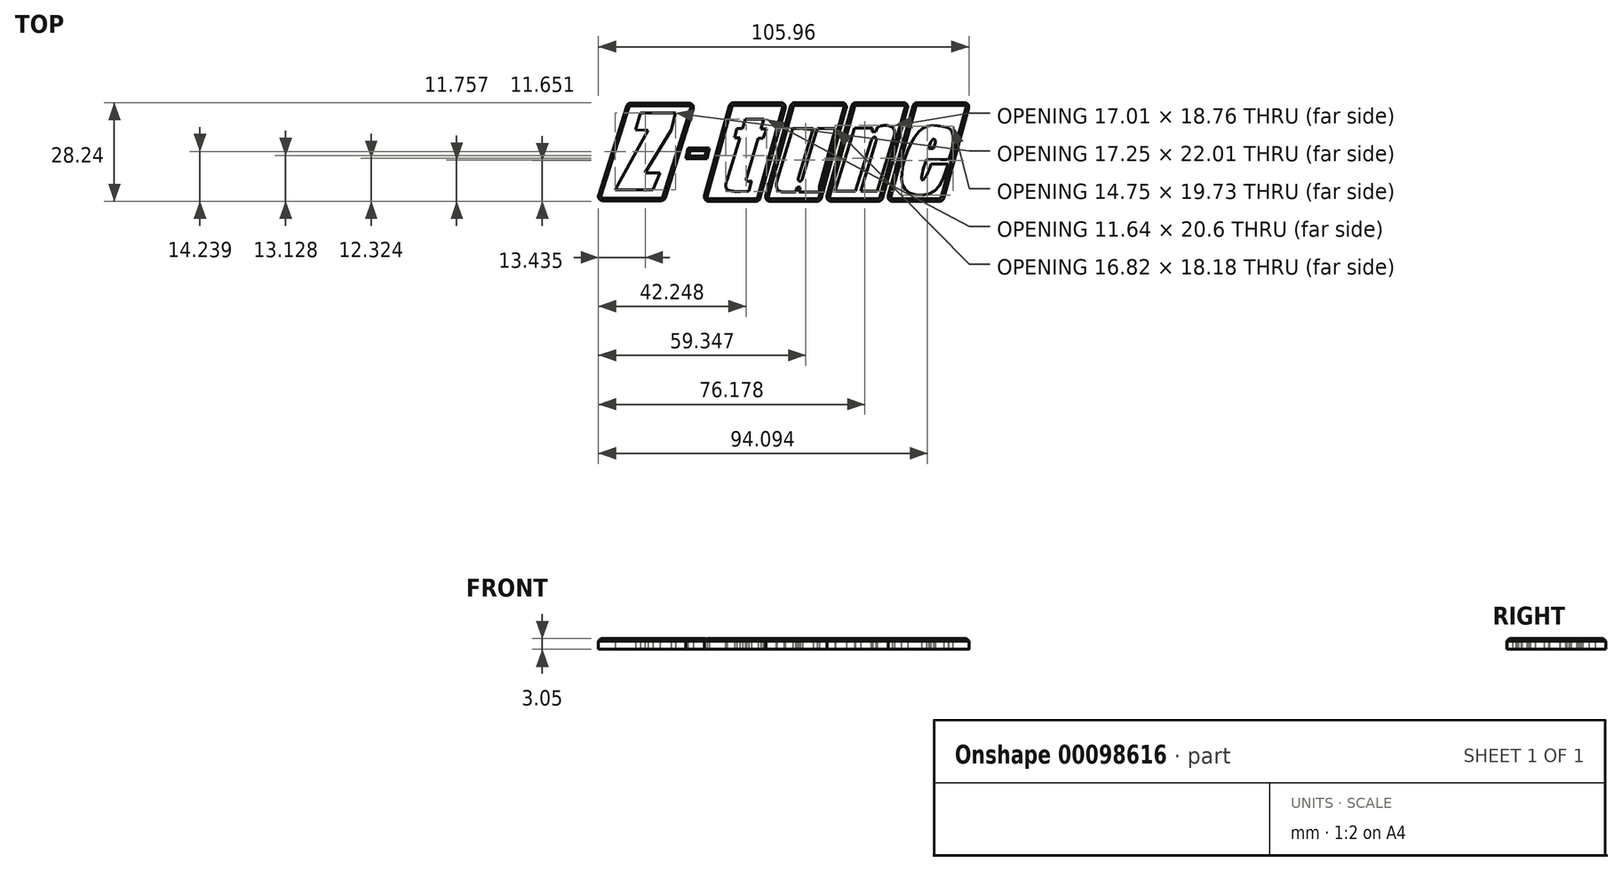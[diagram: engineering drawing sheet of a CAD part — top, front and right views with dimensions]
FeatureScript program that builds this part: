
annotation { "Feature Type Name" : "Feature", "Feature Type Description" : "" }
export const myFeature = defineFeature(function(context is Context, id is Id, definition is map)
    precondition{}
    {
        {
            var Q0;
            Q0=qCreatedBy(makeId("Top.planeOp"),FACE);
            var sketch = newSketch(context, id + "F0", { "sketchPlane" : qUnion([Q0])});
            skLineSegment(sketch, "E0", {"start": v(-41.76, 14.47) * mm, "end": v(-25.09, 14.47) * mm});
            skLineSegment(sketch, "E1", {"start": v(-23.88, 12.82) * mm, "end": v(-31.88, -12.54) * mm});
            skLineSegment(sketch, "E2", {"start": v(-33.1, -13.42) * mm, "end": v(-49.76, -13.42) * mm});
            skLineSegment(sketch, "E3", {"start": v(-50.97, -11.77) * mm, "end": v(-42.97, 13.58) * mm});
            skLineSegment(sketch, "E4", {"start": v(-12.31, 14.64) * mm, "end": v(1.14, 14.64) * mm});
            skLineSegment(sketch, "E5", {"start": v(2.36, 13.03) * mm, "end": v(-4.76, -12.67) * mm});
            skLineSegment(sketch, "E6", {"start": v(-5.99, -13.6) * mm, "end": v(-19.43, -13.6) * mm});
            skLineSegment(sketch, "E7", {"start": v(-20.65, -12) * mm, "end": v(-13.54, 13.7) * mm});
            skPoint(sketch, "E8.visualSharp", {"position": v(-13.28, 14.64) * mm});
            skArc(sketch, "E8.filletArc", {"start": v(-12.31, 14.64) * mm, "mid": v(-13.08, 14.38) * mm, "end": v(-13.54, 13.7) * mm});
            skPoint(sketch, "E9.visualSharp", {"position": v(2.8, 14.64) * mm});
            skArc(sketch, "E9.filletArc", {"start": v(2.36, 13.03) * mm, "mid": v(2.15, 14.14) * mm, "end": v(1.14, 14.64) * mm});
            skPoint(sketch, "E10.visualSharp", {"position": v(-5.02, -13.6) * mm});
            skArc(sketch, "E10.filletArc", {"start": v(-5.99, -13.6) * mm, "mid": v(-5.22, -13.34) * mm, "end": v(-4.76, -12.67) * mm});
            skPoint(sketch, "E11.visualSharp", {"position": v(-21.1, -13.6) * mm});
            skArc(sketch, "E11.filletArc", {"start": v(-20.65, -12) * mm, "mid": v(-20.44, -13.1) * mm, "end": v(-19.43, -13.6) * mm});
            skPoint(sketch, "E12.visualSharp", {"position": v(-23.36, 14.47) * mm});
            skArc(sketch, "E12.filletArc", {"start": v(-23.88, 12.82) * mm, "mid": v(-24.06, 13.95) * mm, "end": v(-25.09, 14.47) * mm});
            skPoint(sketch, "E13.visualSharp", {"position": v(-51.49, -13.42) * mm});
            skArc(sketch, "E13.filletArc", {"start": v(-50.97, -11.77) * mm, "mid": v(-50.78, -12.9) * mm, "end": v(-49.76, -13.42) * mm});
            skPoint(sketch, "E14.visualSharp", {"position": v(-42.7, 14.47) * mm});
            skArc(sketch, "E14.filletArc", {"start": v(-41.76, 14.47) * mm, "mid": v(-42.51, 14.23) * mm, "end": v(-42.97, 13.58) * mm});
            skPoint(sketch, "E15.visualSharp", {"position": v(-32.16, -13.42) * mm});
            skArc(sketch, "E15.filletArc", {"start": v(-33.1, -13.42) * mm, "mid": v(-32.34, -13.18) * mm, "end": v(-31.88, -12.54) * mm});
            skLineSegment(sketch, "E16.1.0.0", {"start": v(19.87, 13.03) * mm, "end": v(12.74, -12.67) * mm});
            skPoint(sketch, "E16.1.0.1", {"position": v(12.49, -13.6) * mm});
            skLineSegment(sketch, "E16.1.0.2", {"start": v(-3.15, -12) * mm, "end": v(3.97, 13.7) * mm});
            skPoint(sketch, "E16.1.0.3", {"position": v(4.23, 14.64) * mm});
            skPoint(sketch, "E16.1.0.4", {"position": v(20.31, 14.64) * mm});
            skLineSegment(sketch, "E16.1.0.5", {"start": v(11.52, -13.6) * mm, "end": v(-1.92, -13.6) * mm});
            skLineSegment(sketch, "E16.1.0.6", {"start": v(5.2, 14.64) * mm, "end": v(18.64, 14.64) * mm});
            skArc(sketch, "E16.1.0.7", {"start": v(-3.15, -12) * mm, "mid": v(-2.93, -13.1) * mm, "end": v(-1.92, -13.6) * mm});
            skArc(sketch, "E16.1.0.8", {"start": v(19.87, 13.03) * mm, "mid": v(19.66, 14.14) * mm, "end": v(18.64, 14.64) * mm});
            skArc(sketch, "E16.1.0.9", {"start": v(5.2, 14.64) * mm, "mid": v(4.42, 14.38) * mm, "end": v(3.97, 13.7) * mm});
            skArc(sketch, "E16.1.0.10", {"start": v(11.52, -13.6) * mm, "mid": v(12.29, -13.34) * mm, "end": v(12.74, -12.67) * mm});
            skLineSegment(sketch, "E16.2.0.0", {"start": v(37.38, 13.03) * mm, "end": v(30.25, -12.67) * mm});
            skPoint(sketch, "E16.2.0.1", {"position": v(30, -13.6) * mm});
            skLineSegment(sketch, "E16.2.0.2", {"start": v(14.36, -12) * mm, "end": v(21.48, 13.7) * mm});
            skPoint(sketch, "E16.2.0.3", {"position": v(21.74, 14.64) * mm});
            skPoint(sketch, "E16.2.0.4", {"position": v(37.82, 14.64) * mm});
            skLineSegment(sketch, "E16.2.0.5", {"start": v(29.03, -13.6) * mm, "end": v(15.59, -13.6) * mm});
            skLineSegment(sketch, "E16.2.0.6", {"start": v(22.7, 14.64) * mm, "end": v(36.15, 14.64) * mm});
            skArc(sketch, "E16.2.0.7", {"start": v(14.36, -12) * mm, "mid": v(14.57, -13.1) * mm, "end": v(15.59, -13.6) * mm});
            skArc(sketch, "E16.2.0.8", {"start": v(37.38, 13.03) * mm, "mid": v(37.16, 14.14) * mm, "end": v(36.15, 14.64) * mm});
            skArc(sketch, "E16.2.0.9", {"start": v(22.7, 14.64) * mm, "mid": v(21.93, 14.38) * mm, "end": v(21.48, 13.7) * mm});
            skArc(sketch, "E16.2.0.10", {"start": v(29.03, -13.6) * mm, "mid": v(29.8, -13.34) * mm, "end": v(30.25, -12.67) * mm});
            skLineSegment(sketch, "E16.3.0.0", {"start": v(54.88, 13.03) * mm, "end": v(47.76, -12.67) * mm});
            skPoint(sketch, "E16.3.0.1", {"position": v(47.5, -13.6) * mm});
            skLineSegment(sketch, "E16.3.0.2", {"start": v(31.87, -12) * mm, "end": v(38.99, 13.7) * mm});
            skPoint(sketch, "E16.3.0.3", {"position": v(39.24, 14.64) * mm});
            skPoint(sketch, "E16.3.0.4", {"position": v(55.33, 14.64) * mm});
            skLineSegment(sketch, "E16.3.0.5", {"start": v(46.54, -13.6) * mm, "end": v(33.1, -13.6) * mm});
            skLineSegment(sketch, "E16.3.0.6", {"start": v(40.2, 14.64) * mm, "end": v(53.66, 14.64) * mm});
            skArc(sketch, "E16.3.0.7", {"start": v(31.87, -12) * mm, "mid": v(32.08, -13.1) * mm, "end": v(33.1, -13.6) * mm});
            skArc(sketch, "E16.3.0.8", {"start": v(54.88, 13.03) * mm, "mid": v(54.67, 14.14) * mm, "end": v(53.66, 14.64) * mm});
            skArc(sketch, "E16.3.0.9", {"start": v(40.2, 14.64) * mm, "mid": v(39.44, 14.38) * mm, "end": v(38.99, 13.7) * mm});
            skArc(sketch, "E16.3.0.10", {"start": v(46.54, -13.6) * mm, "mid": v(47.3, -13.34) * mm, "end": v(47.76, -12.67) * mm});
            skLineSegment(sketch, "E16.direction1", {"start": v(-19.43, -13.6) * mm, "end": v(-1.92, -13.6) * mm, "construction": true});
            skLineSegment(sketch, "E17", {"start": v(-40.42, 6.88) * mm, "end": v(-39, 11.64) * mm});
            skLineSegment(sketch, "E18", {"start": v(-39, 11.64) * mm, "end": v(-28.97, 11.64) * mm});
            skLineSegment(sketch, "E19", {"start": v(-28.97, 11.64) * mm, "end": v(-30.2, 6.7) * mm});
            skLineSegment(sketch, "E20", {"start": v(-30.2, 6.7) * mm, "end": v(-37.74, -5.5) * mm});
            skLineSegment(sketch, "E21", {"start": v(-37.74, -5.5) * mm, "end": v(-33.45, -5.5) * mm});
            skLineSegment(sketch, "E22", {"start": v(-33.45, -5.5) * mm, "end": v(-35.43, -10.36) * mm});
            skLineSegment(sketch, "E23", {"start": v(-35.43, -10.36) * mm, "end": v(-46.22, -10.36) * mm});
            skLineSegment(sketch, "E24", {"start": v(-46.22, -10.36) * mm, "end": v(-36.82, 6.7) * mm});
            skLineSegment(sketch, "E25", {"start": v(-36.82, 6.7) * mm, "end": v(-40.42, 6.88) * mm});
            skLineSegment(sketch, "E26", {"start": v(-9.83, 7.17) * mm, "end": v(-11.48, 7.17) * mm});
            skLineSegment(sketch, "E27", {"start": v(-11.48, 7.17) * mm, "end": v(-12.12, 4.57) * mm});
            skLineSegment(sketch, "E28", {"start": v(-12.12, 4.57) * mm, "end": v(-10.6, 4.57) * mm});
            skLineSegment(sketch, "E29", {"start": v(-10.6, 4.57) * mm, "end": v(-14.18, -7.46) * mm});
            skLineSegment(sketch, "E30", {"start": v(-9.83, 7.17) * mm, "end": v(-9.04, 9.83) * mm});
            skLineSegment(sketch, "E31", {"start": v(-9.04, 9.83) * mm, "end": v(-3.75, 9.83) * mm});
            skLineSegment(sketch, "E32", {"start": v(-5.36, 4.41) * mm, "end": v(-8.7, -6.83) * mm});
            skLineSegment(sketch, "E33", {"start": v(-3.75, 9.83) * mm, "end": v(-4.58, 7.04) * mm});
            skLineSegment(sketch, "E34", {"start": v(-4.58, 7.04) * mm, "end": v(-2.96, 7.04) * mm});
            skLineSegment(sketch, "E35", {"start": v(-2.96, 7.04) * mm, "end": v(-3.88, 4.41) * mm});
            skLineSegment(sketch, "E36", {"start": v(-3.88, 4.41) * mm, "end": v(-5.36, 4.41) * mm});
            skFitSpline(sketch, "E37", {"points": [v(-14.18, -7.46) * mm, v(-10.38, -10.76) * mm], "startDerivative": vector(-2.18, -5.53) * mm, "endDerivative": vector(14.86, 0.83) * mm});
            skFitSpline(sketch, "E38", {"points": [v(-8.7, -6.83) * mm, v(-7.2, -7.79) * mm], "startDerivative": vector(-1.22, -3.46) * mm, "endDerivative": vector(2.26, 0.6) * mm});
            skLineSegment(sketch, "E39", {"start": v(-7.2, -7.79) * mm, "end": v(-7.96, -10.64) * mm});
            skLineSegment(sketch, "E40", {"start": v(-7.96, -10.64) * mm, "end": v(-10.38, -10.76) * mm});
            skLineSegment(sketch, "E41", {"start": v(4.51, 7.24) * mm, "end": v(10.38, 7.24) * mm});
            skLineSegment(sketch, "E42", {"start": v(4.51, 7.24) * mm, "end": v(0, -7.93) * mm});
            skLineSegment(sketch, "E43", {"start": v(10.38, 7.24) * mm, "end": v(6.21, -6.76) * mm});
            skLineSegment(sketch, "E44", {"start": v(11.6, 7.25) * mm, "end": v(16.73, 7.25) * mm});
            skLineSegment(sketch, "E45", {"start": v(16.73, 7.25) * mm, "end": v(12.14, -9.3) * mm});
            skLineSegment(sketch, "E46", {"start": v(11.6, 7.25) * mm, "end": v(7.42, -6.85) * mm});
            skFitSpline(sketch, "E47", {"points": [v(6.21, -6.76) * mm, v(7.42, -6.85) * mm], "startDerivative": vector(-1.08, -3.74) * mm, "endDerivative": vector(1.15, 4.7) * mm});
            skFitSpline(sketch, "E48", {"points": [v(0, -7.93) * mm, v(2.1, -10.93) * mm], "startDerivative": vector(-1.2, -6.14) * mm, "endDerivative": vector(5.12, 0.05) * mm});
            skLineSegment(sketch, "E49", {"start": v(2.1, -10.93) * mm, "end": v(5.37, -10.93) * mm});
            skLineSegment(sketch, "E50", {"start": v(5.37, -10.93) * mm, "end": v(5.82, -9.53) * mm});
            skLineSegment(sketch, "E51", {"start": v(5.82, -9.53) * mm, "end": v(6.78, -9.53) * mm});
            skLineSegment(sketch, "E52", {"start": v(6.78, -9.53) * mm, "end": v(6.33, -10.93) * mm});
            skLineSegment(sketch, "E53", {"start": v(6.33, -10.93) * mm, "end": v(12.14, -10.93) * mm});
            skLineSegment(sketch, "E54", {"start": v(12.14, -10.93) * mm, "end": v(12.14, -9.3) * mm});
            skLineSegment(sketch, "E55", {"start": v(16.64, -10.66) * mm, "end": v(22.18, 7.4) * mm});
            skLineSegment(sketch, "E56", {"start": v(22.18, 7.4) * mm, "end": v(27.47, 7.4) * mm});
            skLineSegment(sketch, "E57", {"start": v(27.47, 7.4) * mm, "end": v(27.14, 6.3) * mm});
            skLineSegment(sketch, "E58", {"start": v(27.14, 6.3) * mm, "end": v(28.35, 6.3) * mm});
            skLineSegment(sketch, "E59", {"start": v(28.35, 6.3) * mm, "end": v(28.68, 7.4) * mm});
            skLineSegment(sketch, "E60", {"start": v(16.64, -10.66) * mm, "end": v(22.54, -10.66) * mm});
            skLineSegment(sketch, "E61", {"start": v(22.54, -10.66) * mm, "end": v(26.9, 3.56) * mm});
            skLineSegment(sketch, "E62", {"start": v(28.37, 3.4) * mm, "end": v(24.05, -10.66) * mm});
            skLineSegment(sketch, "E63", {"start": v(24.05, -10.66) * mm, "end": v(28.67, -10.66) * mm});
            skLineSegment(sketch, "E64", {"start": v(28.67, -10.66) * mm, "end": v(32.99, 3.4) * mm});
            skFitSpline(sketch, "E65", {"points": [v(28.68, 7.4) * mm, v(32.99, 3.4) * mm], "startDerivative": vector(-1.06, 1.71) * mm, "endDerivative": vector(-9.08, -19.6) * mm});
            skFitSpline(sketch, "E66", {"points": [v(28.37, 3.4) * mm, v(26.9, 3.56) * mm], "startDerivative": vector(1.03, 4.34) * mm, "endDerivative": vector(-2.28, -5.78) * mm});
            skLineSegment(sketch, "E67", {"start": v(49.2, -1.66) * mm, "end": v(42.82, -1.66) * mm});
            skLineSegment(sketch, "E68", {"start": v(43.45, 1.5) * mm, "end": v(44.9, 1.5) * mm});
            skLineSegment(sketch, "E69", {"start": v(44.9, 1.5) * mm, "end": v(45.4, 3.14) * mm});
            skLineSegment(sketch, "E70", {"start": v(43.45, 1.5) * mm, "end": v(43.96, 3.19) * mm});
            skFitSpline(sketch, "E71", {"points": [v(43.96, 3.19) * mm, v(45.4, 3.14) * mm], "startDerivative": vector(2.57, 5) * mm, "endDerivative": vector(0.07, -3.44) * mm});
            skLineSegment(sketch, "E72", {"start": v(44.06, -2.9) * mm, "end": v(49.02, -2.9) * mm});
            skFitSpline(sketch, "E73", {"points": [v(42.82, -1.66) * mm, v(44.06, -2.9) * mm], "startDerivative": vector(-10.37, -29.12) * mm, "endDerivative": vector(2.37, 11.87) * mm});
            skFitSpline(sketch, "E74", {"points": [v(49.2, -1.66) * mm, v(47.8, 7.72) * mm], "startDerivative": vector(0.72, 1.83) * mm, "endDerivative": vector(-14.57, 0.87) * mm});
            skFitSpline(sketch, "E75", {"points": [v(47.8, 7.72) * mm, v(42.59, 7.72) * mm, v(38.46, 3.03) * mm, v(35.7, -6.36) * mm, v(37.55, -10.92) * mm, v(44.57, -11.03) * mm, v(49.02, -2.9) * mm], "startDerivative": vector(-38.69, 6.4) * mm, "endDerivative": vector(16.3, 52.53) * mm});
            skLineSegment(sketch, "E76", {"start": v(-25.4, 1.68) * mm, "end": v(-26.08, -1.4) * mm});
            skLineSegment(sketch, "E77", {"start": v(-26.08, -1.4) * mm, "end": v(-19.96, -1.4) * mm});
            skLineSegment(sketch, "E78", {"start": v(-19.96, -1.4) * mm, "end": v(-19.27, 1.68) * mm});
            skLineSegment(sketch, "E79", {"start": v(-19.27, 1.68) * mm, "end": v(-25.4, 1.68) * mm});
            skSolve(sketch);
        }
        {
            var Q0;
            Q0=makeQuery(id+"F0.imprint","IMPRINT",FACE,{"disambiguationData":[TD([[makeQuery(id+"F0.imprint","IMPRINT",EDGE,{"derivedFrom":sQuery(id+"F0.wireOp",EDGE,"E0")}),-1.0]])]});
            var Q1;
            Q1=makeQuery(id+"F0.imprint","IMPRINT",FACE,{"disambiguationData":[TD([[makeQuery(id+"F0.imprint","IMPRINT",EDGE,{"derivedFrom":sQuery(id+"F0.wireOp",EDGE,"E4")}),-1.0]])]});
            var Q2;
            Q2=makeQuery(id+"F0.imprint","IMPRINT",FACE,{"disambiguationData":[TD([[makeQuery(id+"F0.imprint","IMPRINT",EDGE,{"derivedFrom":sQuery(id+"F0.wireOp",EDGE,"E16.1.0.0")}),-1.0]])]});
            var Q3;
            Q3=makeQuery(id+"F0.imprint","IMPRINT",FACE,{"disambiguationData":[TD([[makeQuery(id+"F0.imprint","IMPRINT",EDGE,{"derivedFrom":sQuery(id+"F0.wireOp",EDGE,"E16.2.0.0")}),-1.0]])]});
            var Q4;
            Q4=makeQuery(id+"F0.imprint","IMPRINT",FACE,{"disambiguationData":[TD([[makeQuery(id+"F0.imprint","IMPRINT",EDGE,{"derivedFrom":sQuery(id+"F0.wireOp",EDGE,"E16.3.0.0")}),-1.0]])]});
            var Q5;
            Q5=makeQuery(id+"F0.imprint","IMPRINT",FACE,{"disambiguationData":[TD([[makeQuery(id+"F0.imprint","IMPRINT",EDGE,{"derivedFrom":sQuery(id+"F0.wireOp",EDGE,"E68")}),1.0]])]});
            var Q6;
            Q6=makeQuery(id+"F0.imprint","IMPRINT",FACE,{"disambiguationData":[TD([[makeQuery(id+"F0.imprint","IMPRINT",EDGE,{"derivedFrom":sQuery(id+"F0.wireOp",EDGE,"E76")}),1.0]])]});
            extrude(context, id + "F1", {"entities" : qUnion([Q0, Q1, Q2, Q3, Q4, Q5, Q6]), "depth" : 3.05 * mm});
        }
        {
            var Q0;
            Q0=makeQuery(id+"F1.opExtrude","CAP_EDGE",EDGE,{"disambiguationData":[OSD([sQuery(id+"F0.wireOp",EDGE,"E3")])],"isStart":false});
            var Q1;
            Q1=makeQuery(id+"F1.opExtrude","CAP_EDGE",EDGE,{"disambiguationData":[OSD([sQuery(id+"F0.wireOp",EDGE,"E7")])],"isStart":false});
            var Q2;
            Q2=makeQuery(id+"F1.opExtrude","CAP_EDGE",EDGE,{"disambiguationData":[OSD([sQuery(id+"F0.wireOp",EDGE,"E16.1.0.2")])],"isStart":false});
            var Q3;
            Q3=makeQuery(id+"F1.opExtrude","CAP_EDGE",EDGE,{"disambiguationData":[OSD([sQuery(id+"F0.wireOp",EDGE,"E16.2.0.2")])],"isStart":false});
            var Q4;
            Q4=makeQuery(id+"F1.opExtrude","CAP_EDGE",EDGE,{"disambiguationData":[OSD([sQuery(id+"F0.wireOp",EDGE,"E16.3.0.2")])],"isStart":false});
            chamfer(context, id + "F2", {"entities" : qUnion([Q0, Q1, Q2, Q3, Q4]), "width" : 0.76 * mm, "tangentPropagation" : true});
        }
        {
            var Q0;
            Q0=makeQuery(id+"F1.opExtrude","CAP_EDGE",EDGE,{"disambiguationData":[OSD([sQuery(id+"F0.wireOp",EDGE,"E77")])],"isStart":false});
            var Q1;
            Q1=makeQuery(id+"F1.opExtrude","CAP_EDGE",EDGE,{"disambiguationData":[OSD([sQuery(id+"F0.wireOp",EDGE,"E76")])],"isStart":false});
            var Q2;
            Q2=makeQuery(id+"F1.opExtrude","CAP_EDGE",EDGE,{"disambiguationData":[OSD([sQuery(id+"F0.wireOp",EDGE,"E78")])],"isStart":false});
            var Q3;
            Q3=makeQuery(id+"F1.opExtrude","CAP_EDGE",EDGE,{"disambiguationData":[OSD([sQuery(id+"F0.wireOp",EDGE,"E79")])],"isStart":false});
            chamfer(context, id + "F3", {"entities" : qUnion([Q0, Q1, Q2, Q3]), "width" : 0.76 * mm, "tangentPropagation" : true});
        }
    });
